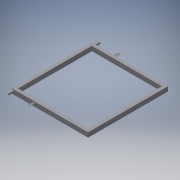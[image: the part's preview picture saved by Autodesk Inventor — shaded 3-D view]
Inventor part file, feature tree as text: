
AUTODESK INVENTOR PART (.ipt)
format: ipt  version: 2018.3 (Build 223284000, 284)  size: 211,456 bytes
history: native  units: mm
features: chamfer x8, extrude x5, sketch x5
ambient origin geometry x8: Origin, YZ Plane, XZ Plane, XY Plane, X Axis, Y Axis, Z Axis, Center Point
bodies: Solid1 (feature_tree)
feature tree (18):
  extrude  "Extrusion1"  Depth=52.5mm
  extrude  "Extrusion2"  Depth=46.0mm
  extrude  "Extrusion5"  Depth=48.5mm TaperAngle=0.0deg
  chamfer  "Chamfer3"  Distance=1.5mm
  chamfer  "Chamfer4"  Distance=1.25mm
  chamfer  "Chamfer5"  Distance=1.0mm
  chamfer  "Chamfer6"  Distance=1.0mm
  extrude  "Extrusion8"  Depth=1.0mm
  chamfer  "Chamfer7"  Distance=1.0mm
  extrude  "Extrusion9"  Depth=1.0mm
  chamfer  "Chamfer8"  Distance=0.5mm
  chamfer  "Chamfer9"  Distance=1.5mm
  chamfer  "Chamfer10"  Distance=4.0mm
  sketch  "Sketch1"  dims[d0=50.0mm d1=52.5mm]
  sketch  "Sketch2"  dims[d2=3.0mm d3=0.0mm d4=46.0mm]
  sketch  "Sketch5"  dims[d5=48.5mm d6=10.0mm d7=0.0mm]
  sketch  "Sketch8"  dims[d24=1.0mm]
  sketch  "Sketch9"  dims[d25=1.0mm d26=1.5mm d27=1.25mm d28=1.0mm d29=1.0mm d30=1.0mm d31=1.0mm d32=1.0mm d33=0.5mm d34=1.5mm d35=4.0mm d36=0.0mm d37=0.288mm d38=2.0mm d39=30.0deg d40=0.288mm d41=2.0mm d42=30.0deg d43=0.499mm d44=2.0mm d45=30.0deg d46=0.499mm d47=2.0mm d48=30.0deg d60=1.0mm d61=30.0deg d62=1.0mm d63=60.0deg d64=1.0mm d65=35.371384mm d66=0.15mm d67=60.0deg d68=0.15mm d69=4.0mm d70=0.0mm d71=0.12mm d72=2.0mm d73=45.0deg d74=1.0mm d75=1.0mm d76=0.5mm d77=1.0mm d78=1.0mm d79=0.5mm d81=1.2mm d82=1.2mm d83=4.0mm d84=0.0mm d85=0.1mm d86=2.0mm d87=45.0deg d88=0.1mm d89=2.0mm d90=45.0deg d91=0.1mm d92=2.0mm d93=45.0deg]
